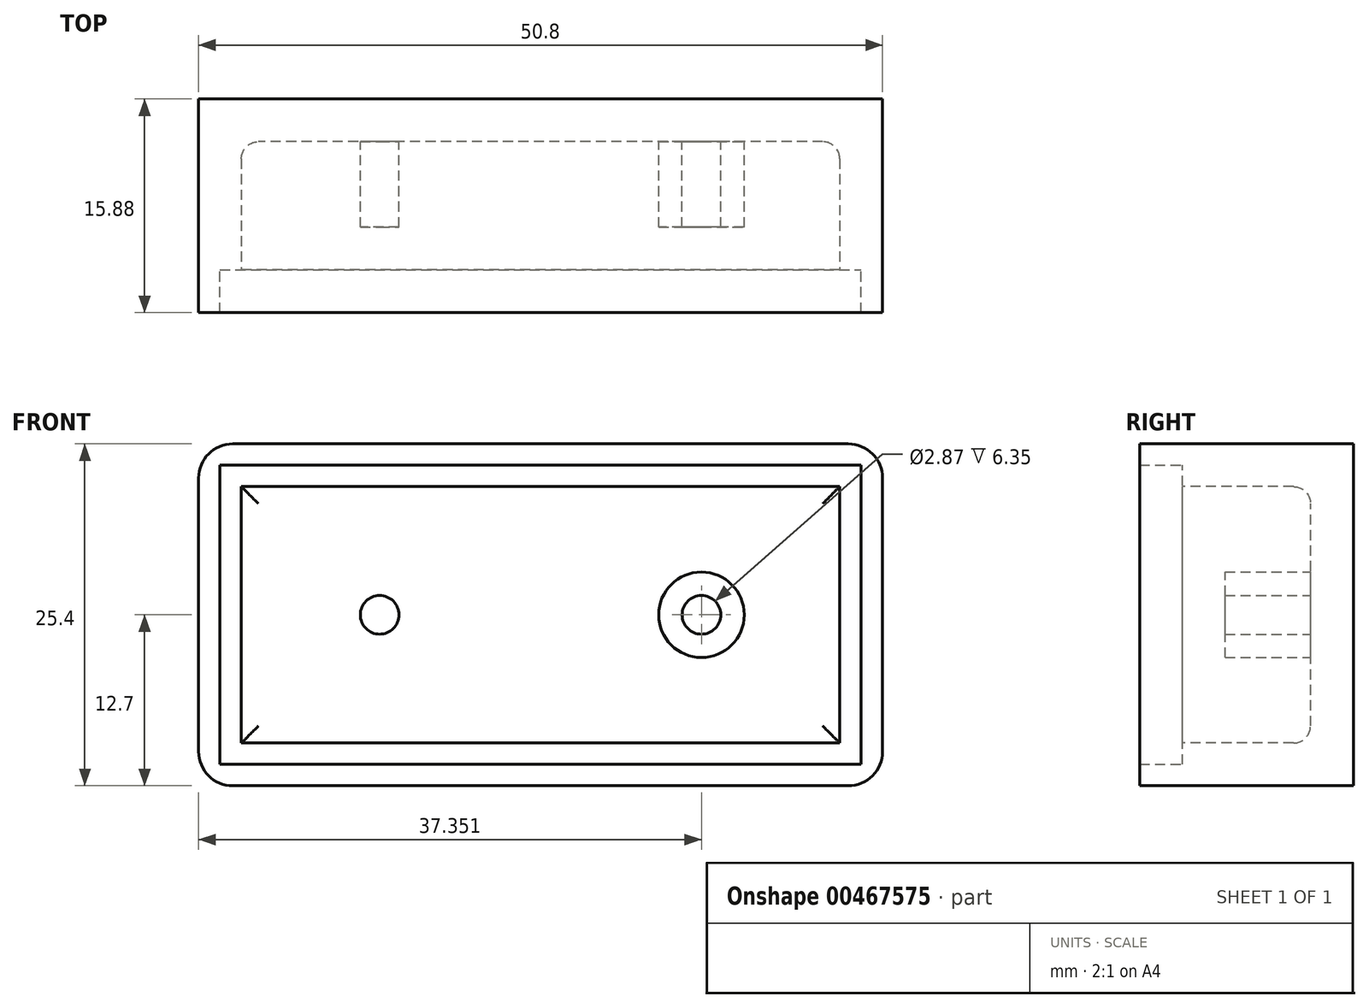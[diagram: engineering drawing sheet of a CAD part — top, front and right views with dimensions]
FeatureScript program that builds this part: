
annotation { "Feature Type Name" : "Feature", "Feature Type Description" : "" }
export const myFeature = defineFeature(function(context is Context, id is Id, definition is map)
    precondition{}
    {
        {
            var Q0;
            Q0=qCreatedBy(makeId("Front.planeOp"),FACE);
            var sketch = newSketch(context, id + "F0", { "sketchPlane" : qUnion([Q0])});
            skLineSegment(sketch, "E0.bottom", {"start": v(25.4, -12.7) * mm, "end": v(-25.4, -12.7) * mm});
            skLineSegment(sketch, "E0.top", {"start": v(25.4, 12.7) * mm, "end": v(-25.4, 12.7) * mm});
            skLineSegment(sketch, "E0.left", {"start": v(25.4, -12.7) * mm, "end": v(25.4, 12.7) * mm});
            skLineSegment(sketch, "E0.right", {"start": v(-25.4, -12.7) * mm, "end": v(-25.4, 12.7) * mm});
            skPoint(sketch, "E0.middle", {"position": v(0, 0) * mm});
            skLineSegment(sketch, "E1.bottom", {"start": v(22.23, -9.52) * mm, "end": v(-22.22, -9.53) * mm});
            skLineSegment(sketch, "E1.top", {"start": v(22.22, 9.53) * mm, "end": v(-22.23, 9.52) * mm});
            skLineSegment(sketch, "E1.left", {"start": v(22.23, -9.52) * mm, "end": v(22.22, 9.53) * mm});
            skLineSegment(sketch, "E1.right", {"start": v(-22.22, -9.53) * mm, "end": v(-22.23, 9.52) * mm});
            skSolve(sketch);
        }
        {
            var Q0;
            Q0=makeQuery(id+"F0.imprint","IMPRINT",FACE,{"disambiguationData":[TD([[makeQuery(id+"F0.imprint","IMPRINT",EDGE,{"derivedFrom":sQuery(id+"F0.wireOp",EDGE,"E0.bottom")}),-1.0]])]});
            var Q1;
            Q1=makeQuery(id+"F0.imprint","IMPRINT",FACE,{"disambiguationData":[TD([[makeQuery(id+"F0.imprint","IMPRINT",EDGE,{"derivedFrom":sQuery(id+"F0.wireOp",EDGE,"E1.bottom")}),-1.0]])]});
            extrude(context, id + "F1", {"entities" : qUnion([Q0, Q1]), "depth" : 12.7 * mm});
        }
        {
            var Q0;
            Q0=makeQuery(id+"F1.opExtrude","CAP_FACE",FACE,{"disambiguationData":[OSD([sQuery(id+"F0.wireOp",EDGE,"E0.bottom"),sQuery(id+"F0.wireOp",EDGE,"E0.top"),sQuery(id+"F0.wireOp",EDGE,"E0.left"),sQuery(id+"F0.wireOp",EDGE,"E0.right")])],"isStart":false});
            var sketch = newSketch(context, id + "F2", { "sketchPlane" : qUnion([Q0])});
            skLineSegment(sketch, "E2.bottom", {"start": v(22.23, -9.52) * mm, "end": v(-22.23, -9.53) * mm});
            skLineSegment(sketch, "E2.top", {"start": v(22.22, 9.53) * mm, "end": v(-22.23, 9.52) * mm});
            skLineSegment(sketch, "E2.left", {"start": v(22.23, -9.52) * mm, "end": v(22.23, 9.53) * mm});
            skLineSegment(sketch, "E2.right", {"start": v(-22.22, -9.53) * mm, "end": v(-22.23, 9.53) * mm});
            skPoint(sketch, "E2.middle", {"position": v(0, 0) * mm});
            skSolve(sketch);
        }
        {
            var Q0;
            Q0 = qSketchRegion(id + "F2", true);
            extrude(context, id + "F3", {"entities" : qUnion([Q0]), "operationType" : NewBodyOperationType.REMOVE, "oppositeDirection" : true, "depth" : 9.52 * mm});
        }
        {
            var Q0;
            Q0=makeQuery(id+"F3.boolean.opBoolean","COPY",EDGE,{"derivedFrom":makeQuery(id+"F3.opExtrude","CAP_EDGE",EDGE,{"disambiguationData":[OSD([sQuery(id+"F2.wireOp",EDGE,"E2.left")])],"isStart":false})});
            var Q1;
            Q1=makeQuery(id+"F3.boolean.opBoolean","COPY",EDGE,{"derivedFrom":makeQuery(id+"F3.opExtrude","CAP_EDGE",EDGE,{"disambiguationData":[OSD([sQuery(id+"F2.wireOp",EDGE,"E2.top")])],"isStart":false})});
            var Q2;
            Q2=makeQuery(id+"F3.boolean.opBoolean","COPY",EDGE,{"derivedFrom":makeQuery(id+"F3.opExtrude","CAP_EDGE",EDGE,{"disambiguationData":[OSD([sQuery(id+"F2.wireOp",EDGE,"E2.right")])],"isStart":false})});
            var Q3;
            Q3=makeQuery(id+"F3.boolean.opBoolean","COPY",EDGE,{"derivedFrom":makeQuery(id+"F3.opExtrude","CAP_EDGE",EDGE,{"disambiguationData":[OSD([sQuery(id+"F2.wireOp",EDGE,"E2.bottom")])],"isStart":false})});
            fillet(context, id + "F4", {"entities" : qUnion([Q0, Q1, Q2, Q3]), "radius" : 1.27 * mm, "tangentPropagation" : true, "allowEdgeOverflow" : false});
        }
        {
            var Q0;
            Q0=makeQuery(id+"F1.opExtrude","CAP_FACE",FACE,{"disambiguationData":[OSD([sQuery(id+"F0.wireOp",EDGE,"E0.bottom"),sQuery(id+"F0.wireOp",EDGE,"E0.top"),sQuery(id+"F0.wireOp",EDGE,"E0.left"),sQuery(id+"F0.wireOp",EDGE,"E0.right")])],"isStart":false});
            var sketch = newSketch(context, id + "F5", { "sketchPlane" : qUnion([Q0])});
            skLineSegment(sketch, "E3.bottom", {"start": v(-23.81, -11.11) * mm, "end": v(23.81, -11.11) * mm});
            skLineSegment(sketch, "E3.top", {"start": v(-23.81, 11.11) * mm, "end": v(23.81, 11.11) * mm});
            skLineSegment(sketch, "E3.left", {"start": v(-23.81, -11.11) * mm, "end": v(-23.81, 11.11) * mm});
            skLineSegment(sketch, "E3.right", {"start": v(23.81, -11.11) * mm, "end": v(23.81, 11.11) * mm});
            skPoint(sketch, "E3.middle", {"position": v(0, 0) * mm});
            skLineSegment(sketch, "E4.bottom", {"start": v(-25.4, -12.7) * mm, "end": v(25.4, -12.7) * mm});
            skLineSegment(sketch, "E4.top", {"start": v(-25.4, 12.7) * mm, "end": v(25.4, 12.7) * mm});
            skLineSegment(sketch, "E4.left", {"start": v(-25.4, -12.7) * mm, "end": v(-25.4, 12.7) * mm});
            skLineSegment(sketch, "E4.right", {"start": v(25.4, -12.7) * mm, "end": v(25.4, 12.7) * mm});
            skSolve(sketch);
        }
        {
            var Q0;
            Q0 = qSketchRegion(id + "F5", true);
            extrude(context, id + "F6", {"entities" : qUnion([Q0]), "operationType" : NewBodyOperationType.ADD, "depth" : 3.17 * mm});
        }
        {
            var Q0;
            Q0=makeQuery(id+"F6.boolean.opBoolean","MERGE",EDGE,{"derivedFrom":[makeQuery(id+"F1.opExtrude","SWEPT_EDGE",EDGE,{"disambiguationData":[OSD([sQuery(id+"F0.wireOp",EDGE,"E0.top"),sQuery(id+"F0.wireOp",EDGE,"E0.left")])]}),makeQuery(id+"F6.opExtrude","SWEPT_EDGE",EDGE,{"disambiguationData":[OSD([sQuery(id+"F5.wireOp",EDGE,"E4.top"),sQuery(id+"F5.wireOp",EDGE,"E4.right")])]})]});
            var Q1;
            Q1=makeQuery(id+"Fb7LW1VqC9DZ5Xq_1.opChamfer","BLEND_EDGE",EDGE,{"blendedFrom":[makeQuery(id+"F1.opExtrude","CAP_EDGE",EDGE,{"disambiguationData":[OSD([sQuery(id+"F0.wireOp",EDGE,"E0.top")])],"isStart":true}),makeQuery(id+"F1.opExtrude","CAP_EDGE",EDGE,{"disambiguationData":[OSD([sQuery(id+"F0.wireOp",EDGE,"E0.left")])],"isStart":true})],"blendedInto":[]});
            var Q2;
            Q2=makeQuery(id+"Fb7LW1VqC9DZ5Xq_1.opChamfer","BLEND_EDGE",EDGE,{"blendedFrom":[makeQuery(id+"F1.opExtrude","CAP_EDGE",EDGE,{"disambiguationData":[OSD([sQuery(id+"F0.wireOp",EDGE,"E0.bottom")])],"isStart":true}),makeQuery(id+"F1.opExtrude","CAP_EDGE",EDGE,{"disambiguationData":[OSD([sQuery(id+"F0.wireOp",EDGE,"E0.left")])],"isStart":true})],"blendedInto":[]});
            var Q3;
            Q3=makeQuery(id+"F6.boolean.opBoolean","MERGE",EDGE,{"derivedFrom":[makeQuery(id+"F1.opExtrude","SWEPT_EDGE",EDGE,{"disambiguationData":[OSD([sQuery(id+"F0.wireOp",EDGE,"E0.bottom"),sQuery(id+"F0.wireOp",EDGE,"E0.left")])]}),makeQuery(id+"F6.opExtrude","SWEPT_EDGE",EDGE,{"disambiguationData":[OSD([sQuery(id+"F5.wireOp",EDGE,"E4.bottom"),sQuery(id+"F5.wireOp",EDGE,"E4.right")])]})]});
            var Q4;
            Q4=makeQuery(id+"Fb7LW1VqC9DZ5Xq_1.opChamfer","BLEND_EDGE",EDGE,{"blendedFrom":[makeQuery(id+"F1.opExtrude","CAP_EDGE",EDGE,{"disambiguationData":[OSD([sQuery(id+"F0.wireOp",EDGE,"E0.bottom")])],"isStart":true}),makeQuery(id+"F1.opExtrude","CAP_EDGE",EDGE,{"disambiguationData":[OSD([sQuery(id+"F0.wireOp",EDGE,"E0.right")])],"isStart":true})],"blendedInto":[]});
            var Q5;
            Q5=makeQuery(id+"F6.boolean.opBoolean","MERGE",EDGE,{"derivedFrom":[makeQuery(id+"F1.opExtrude","SWEPT_EDGE",EDGE,{"disambiguationData":[OSD([sQuery(id+"F0.wireOp",EDGE,"E0.bottom"),sQuery(id+"F0.wireOp",EDGE,"E0.right")])]}),makeQuery(id+"F6.opExtrude","SWEPT_EDGE",EDGE,{"disambiguationData":[OSD([sQuery(id+"F5.wireOp",EDGE,"E4.bottom"),sQuery(id+"F5.wireOp",EDGE,"E4.left")])]})]});
            var Q6;
            Q6=makeQuery(id+"Fb7LW1VqC9DZ5Xq_1.opChamfer","BLEND_EDGE",EDGE,{"blendedFrom":[makeQuery(id+"F1.opExtrude","CAP_EDGE",EDGE,{"disambiguationData":[OSD([sQuery(id+"F0.wireOp",EDGE,"E0.top")])],"isStart":true}),makeQuery(id+"F1.opExtrude","CAP_EDGE",EDGE,{"disambiguationData":[OSD([sQuery(id+"F0.wireOp",EDGE,"E0.right")])],"isStart":true})],"blendedInto":[]});
            var Q7;
            Q7=makeQuery(id+"F6.boolean.opBoolean","MERGE",EDGE,{"derivedFrom":[makeQuery(id+"F1.opExtrude","SWEPT_EDGE",EDGE,{"disambiguationData":[OSD([sQuery(id+"F0.wireOp",EDGE,"E0.top"),sQuery(id+"F0.wireOp",EDGE,"E0.right")])]}),makeQuery(id+"F6.opExtrude","SWEPT_EDGE",EDGE,{"disambiguationData":[OSD([sQuery(id+"F5.wireOp",EDGE,"E4.top"),sQuery(id+"F5.wireOp",EDGE,"E4.left")])]})]});
            fillet(context, id + "F7", {"entities" : qUnion([Q0, Q1, Q2, Q3, Q4, Q5, Q6, Q7]), "radius" : 2.54 * mm, "tangentPropagation" : true, "allowEdgeOverflow" : false});
        }
        {
            var Q0;
            Q0=makeQuery(id+"F3.boolean.opBoolean","COPY",FACE,{"derivedFrom":makeQuery(id+"F3.opExtrude","CAP_FACE",FACE,{"disambiguationData":[OSD([sQuery(id+"F2.wireOp",EDGE,"E2.bottom"),sQuery(id+"F2.wireOp",EDGE,"E2.top"),sQuery(id+"F2.wireOp",EDGE,"E2.left"),sQuery(id+"F2.wireOp",EDGE,"E2.right")])],"isStart":false})});
            var sketch = newSketch(context, id + "F8", { "sketchPlane" : qUnion([Q0])});
            skCircle(sketch, "E5", {"center": v(11.95, 0) * mm, "radius": 3.18 * mm});
            skCircle(sketch, "E6", {"center": v(11.95, 0) * mm, "radius": 1.44 * mm});
            skCircle(sketch, "E7.MirrorC", {"center": v(-11.95, 0) * mm, "radius": 1.44 * mm});
            skCircle(sketch, "E8.MirrorC", {"center": v(-11.95, 0) * mm, "radius": 3.18 * mm});
            skSolve(sketch);
        }
        {
            var Q0;
            Q0=makeQuery(id+"F8.imprint","IMPRINT",FACE,{"disambiguationData":[TD([[makeQuery(id+"F8.imprint","IMPRINT",EDGE,{"derivedFrom":sQuery(id+"F8.wireOp",EDGE,"E5")}),1.0]])]});
            var Q1;
            Q1=makeQuery(id+"F8.imprint","IMPRINT",FACE,{"disambiguationData":[TD([[makeQuery(id+"F8.imprint","IMPRINT",EDGE,{"derivedFrom":sQuery(id+"F8.wireOp",EDGE,"E7.MirrorC")}),1.0]])]});
            var Q2;
            Q2=sQuery(id+"F8.wireOp",EDGE,"E5");
            var Q3;
            Q3=sQuery(id+"F8.wireOp",EDGE,"E8.MirrorC");
            extrude(context, id + "F9", {"entities" : qUnion([Q0, Q1]), "operationType" : NewBodyOperationType.ADD, "surfaceEntities" : qUnion([Q2, Q3]), "depth" : 6.35 * mm});
        }
    });
